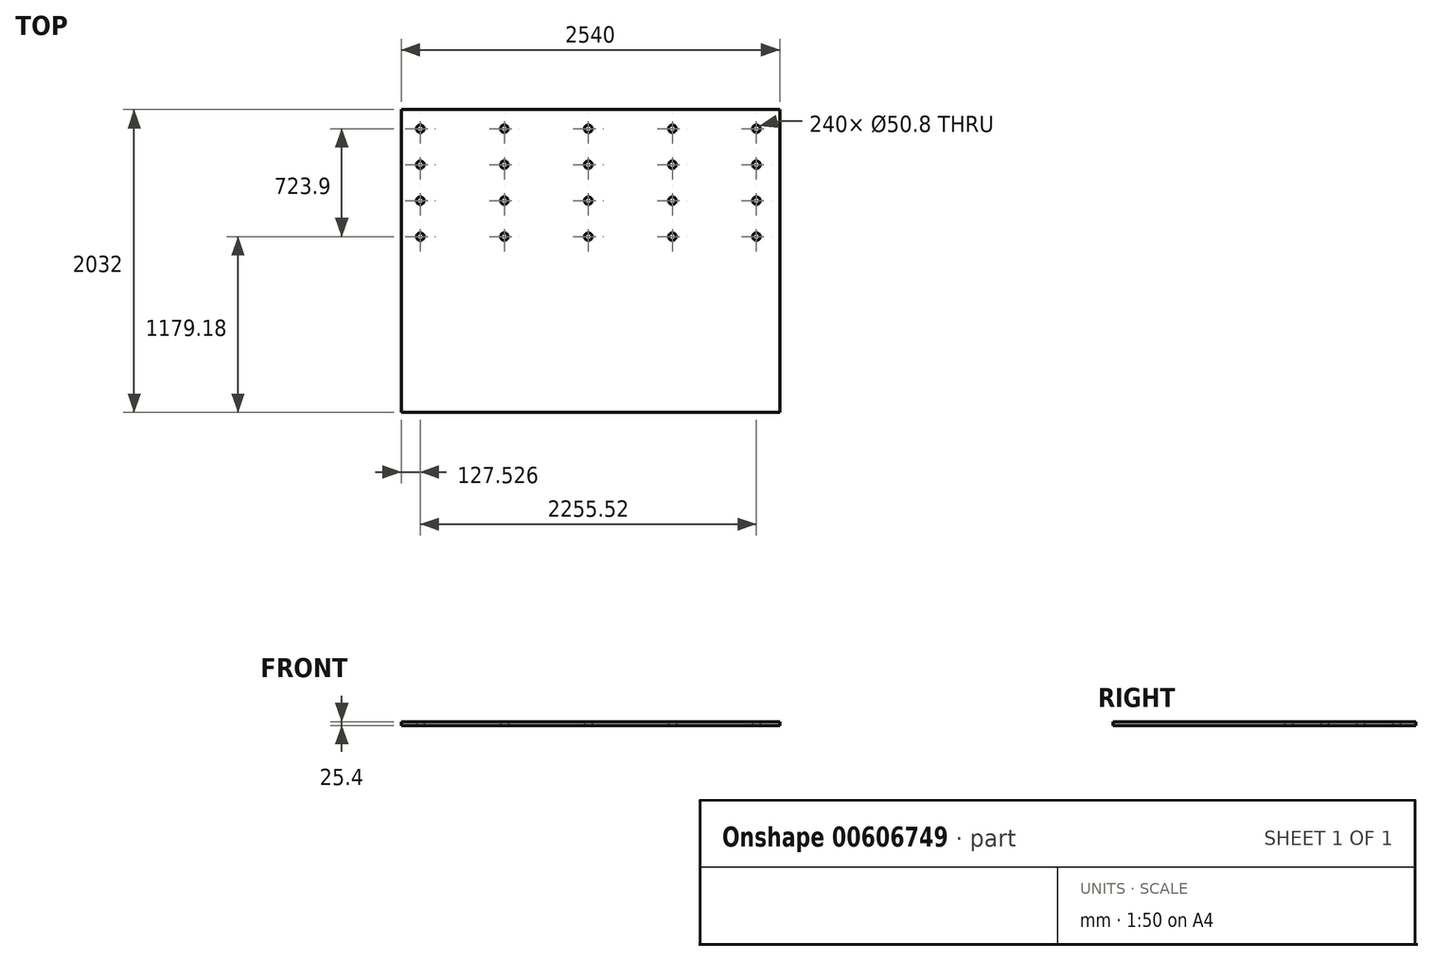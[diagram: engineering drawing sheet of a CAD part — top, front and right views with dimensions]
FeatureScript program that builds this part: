
annotation { "Feature Type Name" : "Feature", "Feature Type Description" : "" }
export const myFeature = defineFeature(function(context is Context, id is Id, definition is map)
    precondition{}
    {
        {
            var Q0;
            Q0=qCreatedBy(makeId("Top.planeOp"),FACE);
            var sketch = newSketch(context, id + "F0", { "sketchPlane" : qUnion([Q0])});
            skLineSegment(sketch, "E0.bottom", {"start": v(0, 0) * mm, "end": v(2540, 0) * mm});
            skLineSegment(sketch, "E0.top", {"start": v(0, 2032) * mm, "end": v(2540, 2032) * mm});
            skLineSegment(sketch, "E0.left", {"start": v(0, 0) * mm, "end": v(0, 2032) * mm});
            skLineSegment(sketch, "E0.right", {"start": v(2540, 0) * mm, "end": v(2540, 2032) * mm});
            skCircle(sketch, "E1", {"center": v(127.53, 1903.08) * mm, "radius": 25.4 * mm});
            skCircle(sketch, "E2.0.1.0", {"center": v(127.53, 1661.78) * mm, "radius": 25.4 * mm});
            skCircle(sketch, "E2.0.2.0", {"center": v(127.53, 1420.48) * mm, "radius": 25.4 * mm});
            skCircle(sketch, "E2.0.3.0", {"center": v(127.53, 1179.18) * mm, "radius": 25.4 * mm});
            skCircle(sketch, "E2.1.0.0", {"center": v(691.4, 1903.08) * mm, "radius": 25.4 * mm});
            skCircle(sketch, "E2.1.1.0", {"center": v(691.4, 1661.78) * mm, "radius": 25.4 * mm});
            skCircle(sketch, "E2.1.2.0", {"center": v(691.4, 1420.48) * mm, "radius": 25.4 * mm});
            skCircle(sketch, "E2.1.3.0", {"center": v(691.4, 1179.18) * mm, "radius": 25.4 * mm});
            skCircle(sketch, "E2.2.0.0", {"center": v(1255.29, 1903.08) * mm, "radius": 25.4 * mm});
            skCircle(sketch, "E2.2.1.0", {"center": v(1255.29, 1661.78) * mm, "radius": 25.4 * mm});
            skCircle(sketch, "E2.2.2.0", {"center": v(1255.29, 1420.48) * mm, "radius": 25.4 * mm});
            skCircle(sketch, "E2.2.3.0", {"center": v(1255.29, 1179.18) * mm, "radius": 25.4 * mm});
            skCircle(sketch, "E2.3.0.0", {"center": v(1819.17, 1903.08) * mm, "radius": 25.4 * mm});
            skCircle(sketch, "E2.3.1.0", {"center": v(1819.17, 1661.78) * mm, "radius": 25.4 * mm});
            skCircle(sketch, "E2.3.2.0", {"center": v(1819.17, 1420.48) * mm, "radius": 25.4 * mm});
            skCircle(sketch, "E2.3.3.0", {"center": v(1819.17, 1179.18) * mm, "radius": 25.4 * mm});
            skCircle(sketch, "E2.4.0.0", {"center": v(2383.05, 1903.08) * mm, "radius": 25.4 * mm});
            skCircle(sketch, "E2.4.1.0", {"center": v(2383.05, 1661.78) * mm, "radius": 25.4 * mm});
            skCircle(sketch, "E2.4.2.0", {"center": v(2383.05, 1420.48) * mm, "radius": 25.4 * mm});
            skCircle(sketch, "E2.4.3.0", {"center": v(2383.05, 1179.18) * mm, "radius": 25.4 * mm});
            skLineSegment(sketch, "E2.direction1", {"start": v(127.53, 1903.08) * mm, "end": v(691.4, 1903.08) * mm, "construction": true});
            skLineSegment(sketch, "E2.direction2", {"start": v(127.53, 1903.08) * mm, "end": v(127.53, 1661.78) * mm, "construction": true});
            skSolve(sketch);
        }
        {
            var Q0;
            Q0 = qSketchRegion(id + "F0", true);
            extrude(context, id + "F1", {"entities" : qUnion([Q0]), "depth" : 25.4 * mm, "offsetDistance" : 25.4 * mm});
        }
    });
